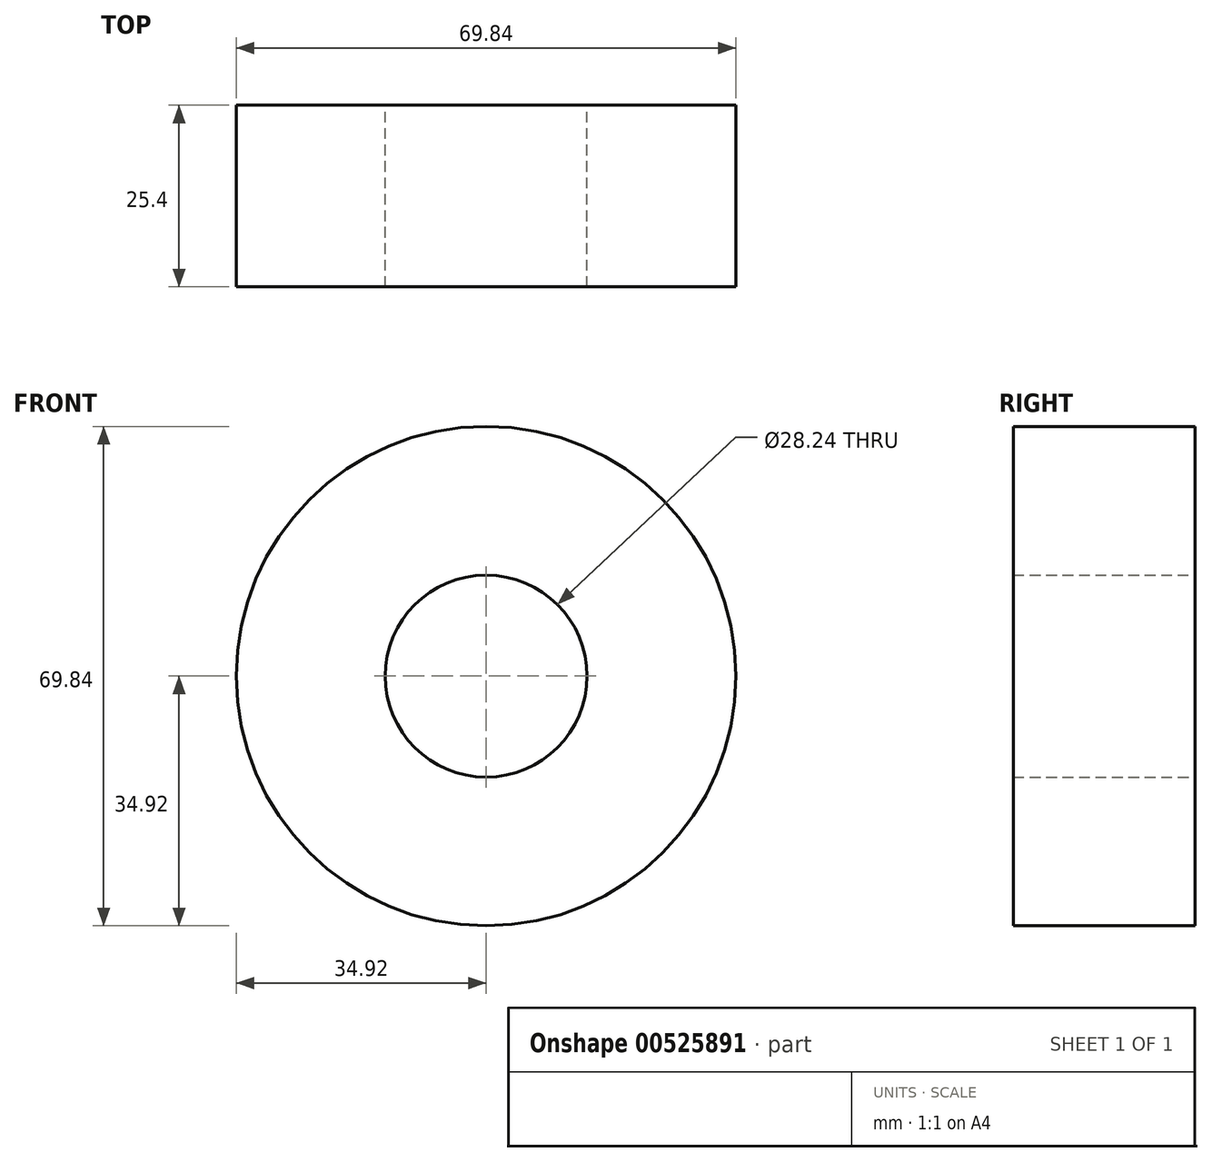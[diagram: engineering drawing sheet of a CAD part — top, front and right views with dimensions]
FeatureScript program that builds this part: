
annotation { "Feature Type Name" : "Feature", "Feature Type Description" : "" }
export const myFeature = defineFeature(function(context is Context, id is Id, definition is map)
    precondition{}
    {
        {
            var Q0;
            Q0=qCreatedBy(makeId("Front.planeOp"),FACE);
            var sketch = newSketch(context, id + "F0", { "sketchPlane" : qUnion([Q0])});
            skCircle(sketch, "E0", {"center": v(0, 0) * mm, "radius": 34.92 * mm});
            skCircle(sketch, "E1", {"center": v(0, 0) * mm, "radius": 14.12 * mm});
            skSolve(sketch);
        }
        {
            var Q0;
            Q0 = qSketchRegion(id + "F0", true);
            extrude(context, id + "F1", {"entities" : qUnion([Q0]), "depth" : 25.4 * mm, "offsetDistance" : 25.4 * mm});
        }
    });
